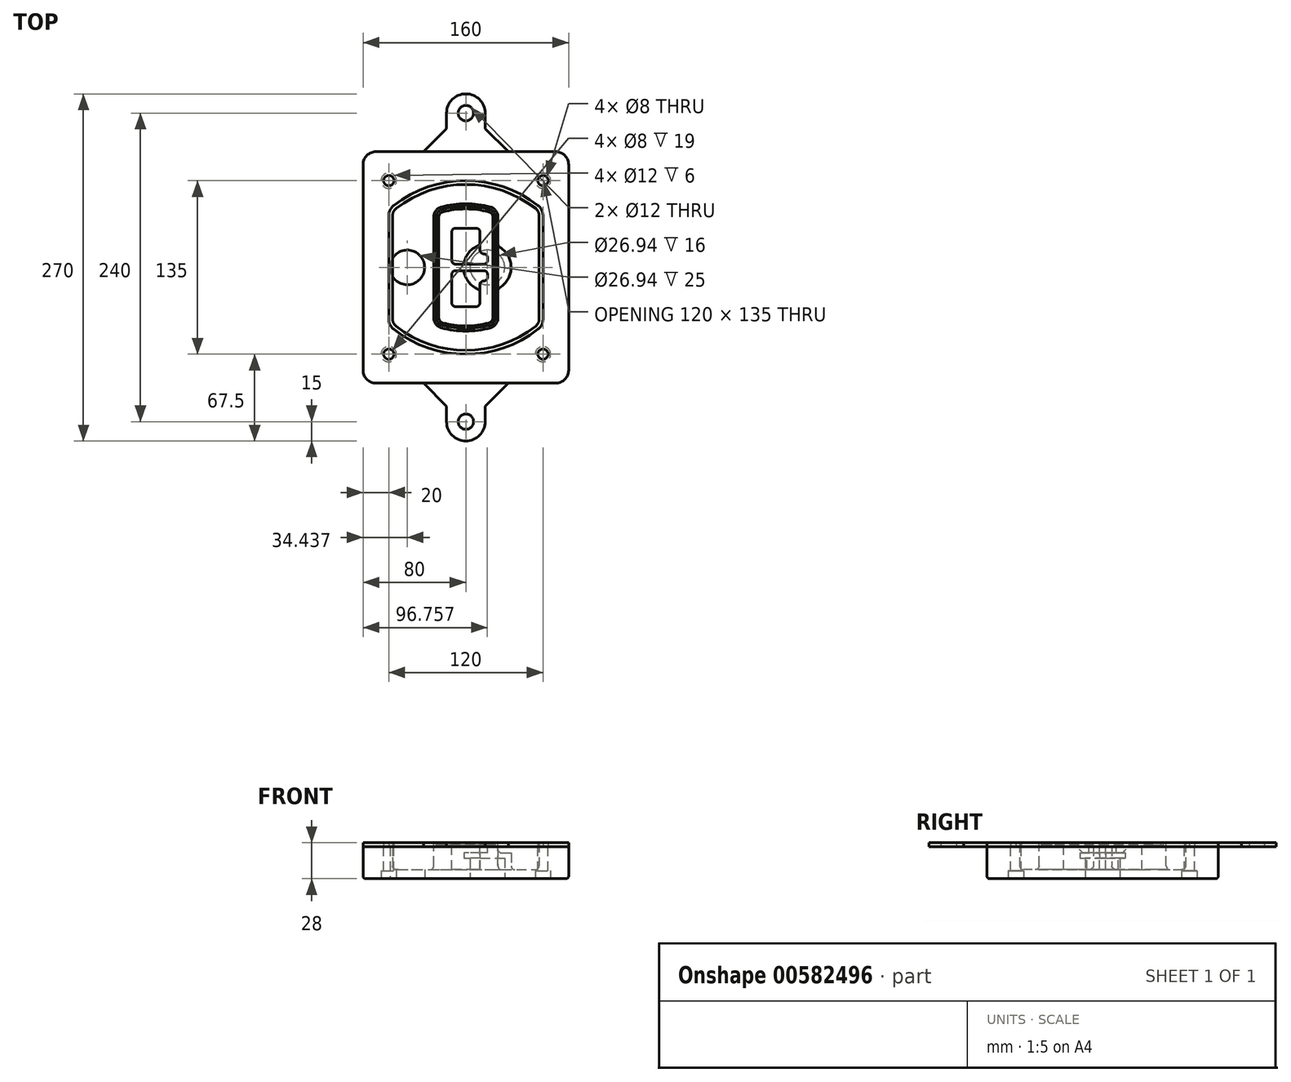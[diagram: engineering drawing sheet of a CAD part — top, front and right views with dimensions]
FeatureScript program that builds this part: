
annotation { "Feature Type Name" : "Feature", "Feature Type Description" : "" }
export const myFeature = defineFeature(function(context is Context, id is Id, definition is map)
    precondition{}
    {
        {
            var Q0;
            Q0=qCreatedBy(makeId("Top.planeOp"),FACE);
            var sketch = newSketch(context, id + "F0", { "sketchPlane" : qUnion([Q0])});
            skPoint(sketch, "E0.rect.middle", {"position": v(0, 0) * mm});
            skLineSegment(sketch, "E1.bottom", {"start": v(-70, -90) * mm, "end": v(70, -90) * mm});
            skLineSegment(sketch, "E1.top", {"start": v(-70, 90) * mm, "end": v(70, 90) * mm});
            skLineSegment(sketch, "E1.left", {"start": v(-80, -80) * mm, "end": v(-80, 80) * mm});
            skLineSegment(sketch, "E1.right", {"start": v(80, -80) * mm, "end": v(80, 80) * mm});
            skLineSegment(sketch, "E2", {"start": v(-80, 90) * mm, "end": v(80, -90) * mm, "construction": true});
            skLineSegment(sketch, "E3", {"start": v(80, 90) * mm, "end": v(-80, -90) * mm, "construction": true});
            skCircle(sketch, "E4", {"center": v(-60, 67.5) * mm, "radius": 4 * mm});
            skCircle(sketch, "E5", {"center": v(60, 67.5) * mm, "radius": 4 * mm});
            skCircle(sketch, "E6", {"center": v(60, -67.5) * mm, "radius": 4 * mm});
            skCircle(sketch, "E7", {"center": v(-60, -67.5) * mm, "radius": 4 * mm});
            skLineSegment(sketch, "E8", {"start": v(-60, 67.5) * mm, "end": v(60, 67.5) * mm, "construction": true});
            skLineSegment(sketch, "E9", {"start": v(60, 67.5) * mm, "end": v(60, -67.5) * mm, "construction": true});
            skLineSegment(sketch, "E10", {"start": v(60, -67.5) * mm, "end": v(-60, -67.5) * mm, "construction": true});
            skLineSegment(sketch, "E11", {"start": v(-60, -67.5) * mm, "end": v(-60, 67.5) * mm, "construction": true});
            skLineSegment(sketch, "E12", {"start": v(-60, 40.3) * mm, "end": v(-60, -40.3) * mm});
            skLineSegment(sketch, "E13", {"start": v(60, 40.3) * mm, "end": v(60, -40.3) * mm});
            skArc(sketch, "E14", {"start": v(56.15, 48.18) * mm, "mid": v(0, 67.5) * mm, "end": v(-56.15, 48.18) * mm});
            skArc(sketch, "E15", {"start": v(-56.15, -48.18) * mm, "mid": v(0, -67.5) * mm, "end": v(56.15, -48.18) * mm});
            skLineSegment(sketch, "E16", {"start": v(-60, 0) * mm, "end": v(60, 0) * mm, "construction": true});
            skPoint(sketch, "E17.visualSharp", {"position": v(-60, -45) * mm});
            skArc(sketch, "E17.filletArc", {"start": v(-60, -40.3) * mm, "mid": v(-58.99, -44.68) * mm, "end": v(-56.15, -48.18) * mm});
            skPoint(sketch, "E18.visualSharp", {"position": v(-60, 45) * mm});
            skArc(sketch, "E18.filletArc", {"start": v(-56.15, 48.18) * mm, "mid": v(-58.99, 44.68) * mm, "end": v(-60, 40.3) * mm});
            skPoint(sketch, "E19.visualSharp", {"position": v(60, 45) * mm});
            skArc(sketch, "E19.filletArc", {"start": v(60, 40.3) * mm, "mid": v(58.99, 44.68) * mm, "end": v(56.15, 48.18) * mm});
            skPoint(sketch, "E20.visualSharp", {"position": v(60, -45) * mm});
            skArc(sketch, "E20.filletArc", {"start": v(56.15, -48.18) * mm, "mid": v(58.99, -44.68) * mm, "end": v(60, -40.3) * mm});
            skPoint(sketch, "E21.visualSharp", {"position": v(-80, 90) * mm});
            skArc(sketch, "E21.filletArc", {"start": v(-70, 90) * mm, "mid": v(-77.07, 87.07) * mm, "end": v(-80, 80) * mm});
            skPoint(sketch, "E22.visualSharp", {"position": v(80, 90) * mm});
            skArc(sketch, "E22.filletArc", {"start": v(80, 80) * mm, "mid": v(77.07, 87.07) * mm, "end": v(70, 90) * mm});
            skPoint(sketch, "E23.visualSharp", {"position": v(80, -90) * mm});
            skArc(sketch, "E23.filletArc", {"start": v(70, -90) * mm, "mid": v(77.07, -87.07) * mm, "end": v(80, -80) * mm});
            skPoint(sketch, "E24.visualSharp", {"position": v(-80, -90) * mm});
            skArc(sketch, "E24.filletArc", {"start": v(-80, -80) * mm, "mid": v(-77.07, -87.07) * mm, "end": v(-70, -90) * mm});
            skArc(sketch, "E25.0", {"start": v(57, 40.3) * mm, "mid": v(56.3, 43.36) * mm, "end": v(54.3, 45.81) * mm});
            skLineSegment(sketch, "E25.1", {"start": v(57, 40.3) * mm, "end": v(57, -40.3) * mm});
            skArc(sketch, "E25.2", {"start": v(54.3, -45.81) * mm, "mid": v(56.3, -43.36) * mm, "end": v(57, -40.3) * mm});
            skArc(sketch, "E25.3", {"start": v(-54.3, -45.81) * mm, "mid": v(0, -64.5) * mm, "end": v(54.3, -45.81) * mm});
            skArc(sketch, "E25.4", {"start": v(-57, -40.3) * mm, "mid": v(-56.3, -43.36) * mm, "end": v(-54.3, -45.81) * mm});
            skArc(sketch, "E25.5", {"start": v(54.3, 45.81) * mm, "mid": v(0, 64.5) * mm, "end": v(-54.3, 45.81) * mm});
            skLineSegment(sketch, "E25.6", {"start": v(-57, 40.3) * mm, "end": v(-57, -40.3) * mm});
            skArc(sketch, "E25.7", {"start": v(-54.3, 45.81) * mm, "mid": v(-56.3, 43.36) * mm, "end": v(-57, 40.3) * mm});
            skArc(sketch, "E26.0", {"start": v(-58.62, 51.33) * mm, "mid": v(-62.58, 46.43) * mm, "end": v(-64, 40.3) * mm});
            skArc(sketch, "E26.1", {"start": v(58.62, 51.33) * mm, "mid": v(0, 71.5) * mm, "end": v(-58.62, 51.33) * mm});
            skArc(sketch, "E26.2", {"start": v(64, 40.3) * mm, "mid": v(62.58, 46.43) * mm, "end": v(58.62, 51.33) * mm});
            skLineSegment(sketch, "E26.3", {"start": v(64, 40.3) * mm, "end": v(64, -40.3) * mm});
            skArc(sketch, "E26.4", {"start": v(58.62, -51.33) * mm, "mid": v(62.58, -46.43) * mm, "end": v(64, -40.3) * mm});
            skLineSegment(sketch, "E26.5", {"start": v(-64, 40.3) * mm, "end": v(-64, -40.3) * mm});
            skArc(sketch, "E26.6", {"start": v(-58.62, -51.33) * mm, "mid": v(0, -71.5) * mm, "end": v(58.62, -51.33) * mm});
            skArc(sketch, "E26.7", {"start": v(-64, -40.3) * mm, "mid": v(-62.58, -46.43) * mm, "end": v(-58.62, -51.33) * mm});
            skSolve(sketch);
        }
        {
            var Q0;
            Q0=makeQuery(id+"F0.imprint","IMPRINT",FACE,{"disambiguationData":[TD([[makeQuery(id+"F0.imprint","IMPRINT",EDGE,{"derivedFrom":sQuery(id+"F0.wireOp",EDGE,"E1.bottom")}),1.0]])]});
            var Q1;
            Q1=makeQuery(id+"F0.imprint","IMPRINT",FACE,{"disambiguationData":[TD([[makeQuery(id+"F0.imprint","IMPRINT",EDGE,{"derivedFrom":sQuery(id+"F0.wireOp",EDGE,"E12")}),1.0]])]});
            var Q2;
            Q2=makeQuery(id+"F0.imprint","IMPRINT",FACE,{"disambiguationData":[TD([[makeQuery(id+"F0.imprint","IMPRINT",EDGE,{"derivedFrom":sQuery(id+"F0.wireOp",EDGE,"E25.0")}),1.0]])]});
            var Q3;
            Q3=makeQuery(id+"F0.imprint","IMPRINT",FACE,{"disambiguationData":[TD([[makeQuery(id+"F0.imprint","IMPRINT",EDGE,{"derivedFrom":sQuery(id+"F0.wireOp",EDGE,"E12")}),-1.0]])]});
            extrude(context, id + "F1", {"entities" : qUnion([Q0, Q1, Q2, Q3]), "oppositeDirection" : true, "depth" : 25 * mm});
        }
        {
            var Q0;
            Q0=makeQuery(id+"F0.imprint","IMPRINT",FACE,{"disambiguationData":[TD([[makeQuery(id+"F0.imprint","IMPRINT",EDGE,{"derivedFrom":sQuery(id+"F0.wireOp",EDGE,"E12")}),1.0]])]});
            extrude(context, id + "F2", {"entities" : qUnion([Q0]), "operationType" : NewBodyOperationType.ADD, "depth" : 3 * mm});
        }
        {
            var Q0;
            Q0=makeQuery(id+"F0.imprint","IMPRINT",FACE,{"disambiguationData":[TD([[makeQuery(id+"F0.imprint","IMPRINT",EDGE,{"derivedFrom":sQuery(id+"F0.wireOp",EDGE,"E25.0")}),1.0]])]});
            extrude(context, id + "F3", {"entities" : qUnion([Q0]), "operationType" : NewBodyOperationType.REMOVE, "oppositeDirection" : true, "depth" : 18 * mm});
        }
        {
            var Q0;
            Q0=makeQuery(id+"F2.opExtrude","CAP_FACE",FACE,{"disambiguationData":[OSD([sQuery(id+"F0.wireOp",EDGE,"E12"),sQuery(id+"F0.wireOp",EDGE,"E13"),sQuery(id+"F0.wireOp",EDGE,"E14"),sQuery(id+"F0.wireOp",EDGE,"E15"),sQuery(id+"F0.wireOp",EDGE,"E17.filletArc"),sQuery(id+"F0.wireOp",EDGE,"E18.filletArc"),sQuery(id+"F0.wireOp",EDGE,"E19.filletArc"),sQuery(id+"F0.wireOp",EDGE,"E20.filletArc"),sQuery(id+"F0.wireOp",EDGE,"E25.0"),sQuery(id+"F0.wireOp",EDGE,"E25.1"),sQuery(id+"F0.wireOp",EDGE,"E25.2"),sQuery(id+"F0.wireOp",EDGE,"E25.3"),sQuery(id+"F0.wireOp",EDGE,"E25.4"),sQuery(id+"F0.wireOp",EDGE,"E25.5"),sQuery(id+"F0.wireOp",EDGE,"E25.6"),sQuery(id+"F0.wireOp",EDGE,"E25.7")])],"isStart":false});
            var sketch = newSketch(context, id + "F4", { "sketchPlane" : qUnion([Q0])});
            skArc(sketch, "E27.0", {"start": v(-19.08, -46.97) * mm, "mid": v(0, -49.5) * mm, "end": v(19.08, -46.97) * mm});
            skArc(sketch, "E28.0", {"start": v(19.08, 46.97) * mm, "mid": v(0, 49.5) * mm, "end": v(-19.08, 46.97) * mm});
            skLineSegment(sketch, "E29", {"start": v(-25, 39.25) * mm, "end": v(-25, -39.25) * mm});
            skLineSegment(sketch, "E30", {"start": v(25, 39.25) * mm, "end": v(25, -39.25) * mm});
            skLineSegment(sketch, "E31", {"start": v(-25, 45.1) * mm, "end": v(25, 45.1) * mm, "construction": true});
            skLineSegment(sketch, "E32", {"start": v(-25, -45.1) * mm, "end": v(25, -45.1) * mm, "construction": true});
            skPoint(sketch, "E33.visualSharp", {"position": v(-25, 45.1) * mm});
            skArc(sketch, "E33.filletArc", {"start": v(-19.08, 46.97) * mm, "mid": v(-23.35, 44.11) * mm, "end": v(-25, 39.25) * mm});
            skPoint(sketch, "E34.visualSharp", {"position": v(25, 45.1) * mm});
            skArc(sketch, "E34.filletArc", {"start": v(25, 39.25) * mm, "mid": v(23.35, 44.11) * mm, "end": v(19.08, 46.97) * mm});
            skPoint(sketch, "E35.visualSharp", {"position": v(25, -45.1) * mm});
            skArc(sketch, "E35.filletArc", {"start": v(19.08, -46.97) * mm, "mid": v(23.35, -44.11) * mm, "end": v(25, -39.25) * mm});
            skPoint(sketch, "E36.visualSharp", {"position": v(-25, -45.1) * mm});
            skArc(sketch, "E36.filletArc", {"start": v(-25, -39.25) * mm, "mid": v(-23.35, -44.11) * mm, "end": v(-19.08, -46.97) * mm});
            skArc(sketch, "E37.0", {"start": v(54.3, 45.81) * mm, "mid": v(0, 64.5) * mm, "end": v(-54.3, 45.81) * mm});
            skArc(sketch, "E37.1", {"start": v(-54.3, 45.81) * mm, "mid": v(-56.3, 43.36) * mm, "end": v(-57, 40.3) * mm});
            skLineSegment(sketch, "E37.2", {"start": v(-57, 40.3) * mm, "end": v(-57, -40.3) * mm});
            skArc(sketch, "E37.3", {"start": v(-57, -40.3) * mm, "mid": v(-56.3, -43.36) * mm, "end": v(-54.3, -45.81) * mm});
            skArc(sketch, "E37.4", {"start": v(-54.3, -45.81) * mm, "mid": v(0, -64.5) * mm, "end": v(54.3, -45.81) * mm});
            skArc(sketch, "E37.5", {"start": v(54.3, -45.81) * mm, "mid": v(56.3, -43.36) * mm, "end": v(57, -40.3) * mm});
            skLineSegment(sketch, "E37.6", {"start": v(57, 40.3) * mm, "end": v(57, -40.3) * mm});
            skArc(sketch, "E37.7", {"start": v(57, 40.3) * mm, "mid": v(56.3, 43.36) * mm, "end": v(54.3, 45.81) * mm});
            skLineSegment(sketch, "E38.0", {"start": v(23, 39.25) * mm, "end": v(23, -39.25) * mm});
            skArc(sketch, "E38.1", {"start": v(18.56, -45.04) * mm, "mid": v(21.76, -42.9) * mm, "end": v(23, -39.25) * mm});
            skArc(sketch, "E38.2", {"start": v(-18.56, -45.04) * mm, "mid": v(0, -47.5) * mm, "end": v(18.56, -45.04) * mm});
            skArc(sketch, "E38.3", {"start": v(-23, -39.25) * mm, "mid": v(-21.76, -42.9) * mm, "end": v(-18.56, -45.04) * mm});
            skLineSegment(sketch, "E38.4", {"start": v(-23, 39.25) * mm, "end": v(-23, -39.25) * mm});
            skArc(sketch, "E38.5", {"start": v(23, 39.25) * mm, "mid": v(21.76, 42.9) * mm, "end": v(18.56, 45.04) * mm});
            skArc(sketch, "E38.6", {"start": v(-18.56, 45.04) * mm, "mid": v(-21.76, 42.9) * mm, "end": v(-23, 39.25) * mm});
            skArc(sketch, "E38.7", {"start": v(18.56, 45.04) * mm, "mid": v(0, 47.5) * mm, "end": v(-18.56, 45.04) * mm});
            skArc(sketch, "E39.0", {"start": v(21, 39.25) * mm, "mid": v(20.18, 41.68) * mm, "end": v(18.04, 43.1) * mm});
            skLineSegment(sketch, "E39.1", {"start": v(21, 39.25) * mm, "end": v(21, -39.25) * mm});
            skArc(sketch, "E39.2", {"start": v(18.04, -43.1) * mm, "mid": v(20.18, -41.68) * mm, "end": v(21, -39.25) * mm});
            skArc(sketch, "E39.3", {"start": v(-18.04, -43.1) * mm, "mid": v(0, -45.5) * mm, "end": v(18.04, -43.1) * mm});
            skArc(sketch, "E39.4", {"start": v(-21, -39.25) * mm, "mid": v(-20.18, -41.68) * mm, "end": v(-18.04, -43.1) * mm});
            skArc(sketch, "E39.5", {"start": v(18.04, 43.1) * mm, "mid": v(0, 45.5) * mm, "end": v(-18.04, 43.1) * mm});
            skLineSegment(sketch, "E39.6", {"start": v(-21, 39.25) * mm, "end": v(-21, -39.25) * mm});
            skArc(sketch, "E39.7", {"start": v(-18.04, 43.1) * mm, "mid": v(-20.18, 41.68) * mm, "end": v(-21, 39.25) * mm});
            skLineSegment(sketch, "E40", {"start": v(-25, 0) * mm, "end": v(25, 0) * mm, "construction": true});
            skLineSegment(sketch, "E41", {"start": v(-11, 5.5) * mm, "end": v(-11, 27.5) * mm});
            skLineSegment(sketch, "E42", {"start": v(-8, 30.5) * mm, "end": v(8, 30.5) * mm});
            skLineSegment(sketch, "E43", {"start": v(11, 27.5) * mm, "end": v(11, 13.5) * mm});
            skLineSegment(sketch, "E44", {"start": v(14, 10.5) * mm, "end": v(14, 10.5) * mm});
            skLineSegment(sketch, "E45", {"start": v(17, 7.5) * mm, "end": v(17, 5.5) * mm});
            skLineSegment(sketch, "E46", {"start": v(14, 2.5) * mm, "end": v(-8, 2.5) * mm});
            skPoint(sketch, "E47.visualSharp", {"position": v(-11, 30.5) * mm});
            skArc(sketch, "E47.filletArc", {"start": v(-8, 30.5) * mm, "mid": v(-10.12, 29.62) * mm, "end": v(-11, 27.5) * mm});
            skPoint(sketch, "E48.visualSharp", {"position": v(11, 30.5) * mm});
            skArc(sketch, "E48.filletArc", {"start": v(11, 27.5) * mm, "mid": v(10.12, 29.62) * mm, "end": v(8, 30.5) * mm});
            skPoint(sketch, "E49.visualSharp", {"position": v(11, 10.5) * mm});
            skArc(sketch, "E49.filletArc", {"start": v(11, 13.5) * mm, "mid": v(11.88, 11.38) * mm, "end": v(14, 10.5) * mm});
            skPoint(sketch, "E50.visualSharp", {"position": v(17, 10.5) * mm});
            skArc(sketch, "E50.filletArc", {"start": v(17, 7.5) * mm, "mid": v(16.12, 9.62) * mm, "end": v(14, 10.5) * mm});
            skPoint(sketch, "E51.visualSharp", {"position": v(17, 2.5) * mm});
            skArc(sketch, "E51.filletArc", {"start": v(14, 2.5) * mm, "mid": v(16.12, 3.38) * mm, "end": v(17, 5.5) * mm});
            skPoint(sketch, "E52.visualSharp", {"position": v(-11, 2.5) * mm});
            skArc(sketch, "E52.filletArc", {"start": v(-11, 5.5) * mm, "mid": v(-10.12, 3.38) * mm, "end": v(-8, 2.5) * mm});
            skLineSegment(sketch, "E53.0.MirrorCS", {"start": v(14, -2.5) * mm, "end": v(-8, -2.5) * mm});
            skArc(sketch, "E54.0.MirrorCS", {"start": v(-11, -5.5) * mm, "mid": v(-10.12, -3.38) * mm, "end": v(-8, -2.5) * mm});
            skLineSegment(sketch, "E55.0.MirrorCS", {"start": v(-11, -5.5) * mm, "end": v(-11, -27.5) * mm});
            skArc(sketch, "E56.0.MirrorCS", {"start": v(-8, -30.5) * mm, "mid": v(-10.12, -29.62) * mm, "end": v(-11, -27.5) * mm});
            skLineSegment(sketch, "E57.0.MirrorCS", {"start": v(-8, -30.5) * mm, "end": v(8, -30.5) * mm});
            skArc(sketch, "E58.0.MirrorCS", {"start": v(11, -27.5) * mm, "mid": v(10.12, -29.62) * mm, "end": v(8, -30.5) * mm});
            skLineSegment(sketch, "E59.0.MirrorCS", {"start": v(11, -27.5) * mm, "end": v(11, -13.5) * mm});
            skArc(sketch, "E60.0.MirrorCS", {"start": v(11, -13.5) * mm, "mid": v(11.88, -11.38) * mm, "end": v(14, -10.5) * mm});
            skArc(sketch, "E61.0.MirrorCS", {"start": v(17, -7.5) * mm, "mid": v(16.12, -9.62) * mm, "end": v(14, -10.5) * mm});
            skLineSegment(sketch, "E62.0.MirrorCS", {"start": v(17, -7.5) * mm, "end": v(17, -5.5) * mm});
            skArc(sketch, "E63.0.MirrorCS", {"start": v(14, -2.5) * mm, "mid": v(16.12, -3.38) * mm, "end": v(17, -5.5) * mm});
            skSolve(sketch);
        }
        {
            var Q0;
            Q0=makeQuery(id+"F4.imprint","IMPRINT",FACE,{"disambiguationData":[TD([[makeQuery(id+"F4.imprint","IMPRINT",EDGE,{"derivedFrom":sQuery(id+"F4.wireOp",EDGE,"E27.0")}),1.0]])]});
            var Q1;
            Q1=makeQuery(id+"F4.imprint","IMPRINT",FACE,{"disambiguationData":[TD([[makeQuery(id+"F4.imprint","IMPRINT",EDGE,{"derivedFrom":sQuery(id+"F4.wireOp",EDGE,"E38.0")}),-1.0]])]});
            var Q2;
            Q2=makeQuery(id+"F4.imprint","IMPRINT",FACE,{"disambiguationData":[TD([[makeQuery(id+"F4.imprint","IMPRINT",EDGE,{"derivedFrom":sQuery(id+"F4.wireOp",EDGE,"E39.0")}),1.0]])]});
            extrude(context, id + "F5", {"entities" : qUnion([Q0, Q1, Q2]), "operationType" : NewBodyOperationType.ADD, "endBound" : BoundingType.UP_TO_NEXT, "oppositeDirection" : true, "depth" : 25 * mm});
        }
        {
            var Q0;
            Q0=makeQuery(id+"F4.imprint","IMPRINT",FACE,{"disambiguationData":[TD([[makeQuery(id+"F4.imprint","IMPRINT",EDGE,{"derivedFrom":sQuery(id+"F4.wireOp",EDGE,"E38.0")}),-1.0]])]});
            extrude(context, id + "F6", {"entities" : qUnion([Q0]), "operationType" : NewBodyOperationType.REMOVE, "oppositeDirection" : true, "depth" : 2 * mm});
        }
        {
            var Q0;
            Q0=makeQuery(id+"F1.opExtrude","CAP_FACE",FACE,{"disambiguationData":[OSD([sQuery(id+"F0.wireOp",EDGE,"E1.bottom"),sQuery(id+"F0.wireOp",EDGE,"E1.top"),sQuery(id+"F0.wireOp",EDGE,"E1.left"),sQuery(id+"F0.wireOp",EDGE,"E1.right"),sQuery(id+"F0.wireOp",EDGE,"E4"),sQuery(id+"F0.wireOp",EDGE,"E5"),sQuery(id+"F0.wireOp",EDGE,"E6"),sQuery(id+"F0.wireOp",EDGE,"E7"),sQuery(id+"F0.wireOp",EDGE,"E21.filletArc"),sQuery(id+"F0.wireOp",EDGE,"E22.filletArc"),sQuery(id+"F0.wireOp",EDGE,"E23.filletArc"),sQuery(id+"F0.wireOp",EDGE,"E24.filletArc")])],"isStart":false});
            var sketch = newSketch(context, id + "F7", { "sketchPlane" : qUnion([Q0])});
            skCircle(sketch, "E64", {"center": v(16.76, 0) * mm, "radius": 13.47 * mm});
            skCircle(sketch, "E65", {"center": v(-45.56, 0) * mm, "radius": 13.47 * mm});
            skLineSegment(sketch, "E66", {"start": v(80, 0) * mm, "end": v(-80, 0) * mm});
            skCircle(sketch, "E67", {"center": v(16.76, 0) * mm, "radius": 18.47 * mm});
            skCircle(sketch, "E68", {"center": v(60, -67.5) * mm, "radius": 6 * mm});
            skCircle(sketch, "E69", {"center": v(-60, -67.5) * mm, "radius": 6 * mm});
            skCircle(sketch, "E70", {"center": v(-60, 67.5) * mm, "radius": 6 * mm});
            skCircle(sketch, "E71", {"center": v(60, 67.5) * mm, "radius": 6 * mm});
            skSolve(sketch);
        }
        {
            var Q0;
            {var subQ1=sQuery(id+"F7.wireOp",EDGE,"E66");var subQ4=sQuery(id+"F7.wireOp",EDGE,"E64");var subQ6=makeQuery(id+"F7.imprint","INTERSECT",VERTEX,{"disambiguationData":[OD(0.0)],"derivedFrom":[subQ4,subQ1]});Q0=makeQuery(id+"F7.imprint","IMPRINT",FACE,{"disambiguationData":[TD([[makeQuery(id+"F7.imprint","IMPRINT",EDGE,{"disambiguationData":[TD([[subQ6,-1.0]])],"derivedFrom":subQ4}),-1.0]])]});}
            var Q1;
            {var subQ0=sQuery(id+"F7.wireOp",EDGE,"E66");var subQ1=sQuery(id+"F7.wireOp",EDGE,"E64");var subQ3=makeQuery(id+"F7.imprint","INTERSECT",VERTEX,{"disambiguationData":[OD(0.0)],"derivedFrom":[subQ1,subQ0]});Q1=makeQuery(id+"F7.imprint","IMPRINT",FACE,{"disambiguationData":[TD([[makeQuery(id+"F7.imprint","IMPRINT",EDGE,{"disambiguationData":[TD([[subQ3,-1.0]])],"derivedFrom":subQ1}),1.0]])]});}
            var Q2;
            {var subQ0=sQuery(id+"F7.wireOp",EDGE,"E66");var subQ1=sQuery(id+"F7.wireOp",EDGE,"E64");var subQ3=makeQuery(id+"F7.imprint","INTERSECT",VERTEX,{"disambiguationData":[OD(0.0)],"derivedFrom":[subQ1,subQ0]});Q2=makeQuery(id+"F7.imprint","IMPRINT",FACE,{"disambiguationData":[TD([[makeQuery(id+"F7.imprint","IMPRINT",EDGE,{"disambiguationData":[TD([[subQ3,1.0]])],"derivedFrom":subQ1}),1.0]])]});}
            var Q3;
            {var subQ1=sQuery(id+"F7.wireOp",EDGE,"E66");var subQ4=sQuery(id+"F7.wireOp",EDGE,"E64");var subQ6=makeQuery(id+"F7.imprint","INTERSECT",VERTEX,{"disambiguationData":[OD(0.0)],"derivedFrom":[subQ4,subQ1]});Q3=makeQuery(id+"F7.imprint","IMPRINT",FACE,{"disambiguationData":[TD([[makeQuery(id+"F7.imprint","IMPRINT",EDGE,{"disambiguationData":[TD([[subQ6,1.0]])],"derivedFrom":subQ4}),-1.0]])]});}
            extrude(context, id + "F8", {"entities" : qUnion([Q0, Q1, Q2, Q3]), "operationType" : NewBodyOperationType.ADD, "oppositeDirection" : true, "depth" : 20 * mm});
        }
        {
            var Q0;
            {var subQ0=sQuery(id+"F7.wireOp",EDGE,"E66");var subQ1=sQuery(id+"F7.wireOp",EDGE,"E64");var subQ3=makeQuery(id+"F7.imprint","INTERSECT",VERTEX,{"disambiguationData":[OD(0.0)],"derivedFrom":[subQ1,subQ0]});Q0=makeQuery(id+"F7.imprint","IMPRINT",FACE,{"disambiguationData":[TD([[makeQuery(id+"F7.imprint","IMPRINT",EDGE,{"disambiguationData":[TD([[subQ3,-1.0]])],"derivedFrom":subQ1}),1.0]])]});}
            var Q1;
            {var subQ0=sQuery(id+"F7.wireOp",EDGE,"E66");var subQ1=sQuery(id+"F7.wireOp",EDGE,"E64");var subQ3=makeQuery(id+"F7.imprint","INTERSECT",VERTEX,{"disambiguationData":[OD(0.0)],"derivedFrom":[subQ1,subQ0]});Q1=makeQuery(id+"F7.imprint","IMPRINT",FACE,{"disambiguationData":[TD([[makeQuery(id+"F7.imprint","IMPRINT",EDGE,{"disambiguationData":[TD([[subQ3,1.0]])],"derivedFrom":subQ1}),1.0]])]});}
            extrude(context, id + "F9", {"entities" : qUnion([Q0, Q1]), "operationType" : NewBodyOperationType.REMOVE, "oppositeDirection" : true, "depth" : 16 * mm});
        }
        {
            var Q0;
            {var subQ0=sQuery(id+"F7.wireOp",EDGE,"E66");var subQ1=sQuery(id+"F7.wireOp",EDGE,"E65");var subQ3=makeQuery(id+"F7.imprint","INTERSECT",VERTEX,{"disambiguationData":[OD(0.0)],"derivedFrom":[subQ1,subQ0]});Q0=makeQuery(id+"F7.imprint","IMPRINT",FACE,{"disambiguationData":[TD([[makeQuery(id+"F7.imprint","IMPRINT",EDGE,{"disambiguationData":[TD([[subQ3,-1.0]])],"derivedFrom":subQ1}),1.0]])]});}
            var Q1;
            {var subQ0=sQuery(id+"F7.wireOp",EDGE,"E66");var subQ1=sQuery(id+"F7.wireOp",EDGE,"E65");var subQ3=makeQuery(id+"F7.imprint","INTERSECT",VERTEX,{"disambiguationData":[OD(0.0)],"derivedFrom":[subQ1,subQ0]});Q1=makeQuery(id+"F7.imprint","IMPRINT",FACE,{"disambiguationData":[TD([[makeQuery(id+"F7.imprint","IMPRINT",EDGE,{"disambiguationData":[TD([[subQ3,1.0]])],"derivedFrom":subQ1}),1.0]])]});}
            extrude(context, id + "F10", {"entities" : qUnion([Q0, Q1]), "operationType" : NewBodyOperationType.REMOVE, "oppositeDirection" : true, "depth" : 25 * mm});
        }
        {
            var Q0;
            Q0=makeQuery(id+"F7.imprint","IMPRINT",FACE,{"disambiguationData":[TD([[makeQuery(id+"F7.imprint","IMPRINT",EDGE,{"derivedFrom":sQuery(id+"F7.wireOp",EDGE,"E68")}),1.0]])]});
            var Q1;
            Q1=makeQuery(id+"F7.imprint","IMPRINT",FACE,{"disambiguationData":[TD([[makeQuery(id+"F7.imprint","IMPRINT",EDGE,{"derivedFrom":makeQuery(id+"F1.opExtrude","CAP_EDGE",EDGE,{"disambiguationData":[OSD([sQuery(id+"F0.wireOp",EDGE,"E5")])],"isStart":false})}),-1.0]])]});
            var Q2;
            Q2=makeQuery(id+"F7.imprint","IMPRINT",FACE,{"disambiguationData":[TD([[makeQuery(id+"F7.imprint","IMPRINT",EDGE,{"derivedFrom":sQuery(id+"F7.wireOp",EDGE,"E69")}),1.0]])]});
            var Q3;
            Q3=makeQuery(id+"F7.imprint","IMPRINT",FACE,{"disambiguationData":[TD([[makeQuery(id+"F7.imprint","IMPRINT",EDGE,{"derivedFrom":makeQuery(id+"F1.opExtrude","CAP_EDGE",EDGE,{"disambiguationData":[OSD([sQuery(id+"F0.wireOp",EDGE,"E4")])],"isStart":false})}),-1.0]])]});
            var Q4;
            Q4=makeQuery(id+"F7.imprint","IMPRINT",FACE,{"disambiguationData":[TD([[makeQuery(id+"F7.imprint","IMPRINT",EDGE,{"derivedFrom":sQuery(id+"F7.wireOp",EDGE,"E70")}),1.0]])]});
            var Q5;
            Q5=makeQuery(id+"F7.imprint","IMPRINT",FACE,{"disambiguationData":[TD([[makeQuery(id+"F7.imprint","IMPRINT",EDGE,{"derivedFrom":makeQuery(id+"F1.opExtrude","CAP_EDGE",EDGE,{"disambiguationData":[OSD([sQuery(id+"F0.wireOp",EDGE,"E7")])],"isStart":false})}),-1.0]])]});
            var Q6;
            Q6=makeQuery(id+"F7.imprint","IMPRINT",FACE,{"disambiguationData":[TD([[makeQuery(id+"F7.imprint","IMPRINT",EDGE,{"derivedFrom":sQuery(id+"F7.wireOp",EDGE,"E71")}),1.0]])]});
            var Q7;
            Q7=makeQuery(id+"F7.imprint","IMPRINT",FACE,{"disambiguationData":[TD([[makeQuery(id+"F7.imprint","IMPRINT",EDGE,{"derivedFrom":makeQuery(id+"F1.opExtrude","CAP_EDGE",EDGE,{"disambiguationData":[OSD([sQuery(id+"F0.wireOp",EDGE,"E6")])],"isStart":false})}),-1.0]])]});
            extrude(context, id + "F11", {"entities" : qUnion([Q0, Q1, Q2, Q3, Q4, Q5, Q6, Q7]), "operationType" : NewBodyOperationType.REMOVE, "oppositeDirection" : true, "depth" : 6 * mm});
        }
        {
            var Q0;
            Q0=makeQuery(id+"F9.boolean.opBoolean","COPY",FACE,{"derivedFrom":makeQuery(id+"F9.opExtrude","CAP_FACE",FACE,{"disambiguationData":[OSD([sQuery(id+"F7.wireOp",EDGE,"E64")])],"isStart":false})});
            var sketch = newSketch(context, id + "F12", { "sketchPlane" : qUnion([Q0])});
            skArc(sketch, "E72.0", {"start": v(11, 17.55) * mm, "mid": v(2.57, 11.82) * mm, "end": v(-1.54, 2.5) * mm});
            skArc(sketch, "E72.1", {"start": v(-1.54, -2.5) * mm, "mid": v(2.57, -11.82) * mm, "end": v(11, -17.55) * mm});
            skLineSegment(sketch, "E73", {"start": v(-1.54, -2.5) * mm, "end": v(14, -2.5) * mm});
            skLineSegment(sketch, "E74.0", {"start": v(14, 2.5) * mm, "end": v(-1.54, 2.5) * mm});
            skArc(sketch, "E74.1", {"start": v(14, 2.5) * mm, "mid": v(16.12, 3.38) * mm, "end": v(17, 5.5) * mm});
            skLineSegment(sketch, "E74.2", {"start": v(17, 7.5) * mm, "end": v(17, 5.5) * mm});
            skArc(sketch, "E74.3", {"start": v(17, 7.5) * mm, "mid": v(16.12, 9.62) * mm, "end": v(14, 10.5) * mm});
            skArc(sketch, "E74.4", {"start": v(11, 13.5) * mm, "mid": v(11.88, 11.38) * mm, "end": v(14, 10.5) * mm});
            skLineSegment(sketch, "E74.5", {"start": v(11, 17.55) * mm, "end": v(11, 13.5) * mm});
            skLineSegment(sketch, "E74.7", {"start": v(14, -2.5) * mm, "end": v(-1.54, -2.5) * mm});
            skArc(sketch, "E74.8", {"start": v(14, -2.5) * mm, "mid": v(16.12, -3.38) * mm, "end": v(17, -5.5) * mm});
            skLineSegment(sketch, "E74.9", {"start": v(17, -7.5) * mm, "end": v(17, -5.5) * mm});
            skArc(sketch, "E74.10", {"start": v(17, -7.5) * mm, "mid": v(16.12, -9.62) * mm, "end": v(14, -10.5) * mm});
            skArc(sketch, "E74.11", {"start": v(11, -13.5) * mm, "mid": v(11.88, -11.38) * mm, "end": v(14, -10.5) * mm});
            skLineSegment(sketch, "E74.12", {"start": v(11, -17.55) * mm, "end": v(11, -13.5) * mm});
            skPoint(sketch, "E75.orphan", {"position": v(11, -27.5) * mm});
            skPoint(sketch, "E76.orphan", {"position": v(-8, -2.5) * mm});
            skPoint(sketch, "E77.orphan", {"position": v(-8, 2.5) * mm});
            skPoint(sketch, "E78.orphan", {"position": v(11, 27.5) * mm});
            skSolve(sketch);
        }
        {
            var Q0;
            {var subQ7=sQuery(id+"F12.wireOp",EDGE,"E72.0");var subQ14=sQuery(id+"F12.wireOp",EDGE,"E72.1");var subQ16=sQuery(id+"F12.wireOp",EDGE,"E74.1");var subQ18=sQuery(id+"F12.wireOp",EDGE,"E74.8");Q0=qUnion([makeQuery(id+"F12.imprint","IMPRINT",FACE,{"disambiguationData":[TD([[makeQuery(id+"F12.imprint","IMPRINT",EDGE,{"derivedFrom":subQ7}),1.0]])]}),makeQuery(id+"F12.imprint","IMPRINT",FACE,{"disambiguationData":[TD([[makeQuery(id+"F12.imprint","IMPRINT",EDGE,{"derivedFrom":subQ14}),1.0]])]}),makeQuery(id+"F12.imprint","IMPRINT",FACE,{"disambiguationData":[TD([[makeQuery(id+"F12.imprint","IMPRINT",EDGE,{"derivedFrom":subQ16}),1.0]])]}),makeQuery(id+"F12.imprint","IMPRINT",FACE,{"disambiguationData":[TD([[makeQuery(id+"F12.imprint","IMPRINT",EDGE,{"derivedFrom":subQ18}),-1.0]])]})]);}
            var Q1;
            Q1=makeQuery(id+"F5.boolean.opBoolean","SPLIT",FACE,{"disambiguationData":[TD([makeQuery(id+"F5.opExtrude","SWEPT_FACE",FACE,{"disambiguationData":[OSD([sQuery(id+"F4.wireOp",EDGE,"E41")])]})])],"derivedFrom":makeQuery(id+"F3.boolean.opBoolean","COPY",FACE,{"derivedFrom":makeQuery(id+"F3.opExtrude","CAP_FACE",FACE,{"disambiguationData":[OSD([sQuery(id+"F0.wireOp",EDGE,"E25.0"),sQuery(id+"F0.wireOp",EDGE,"E25.1"),sQuery(id+"F0.wireOp",EDGE,"E25.2"),sQuery(id+"F0.wireOp",EDGE,"E25.3"),sQuery(id+"F0.wireOp",EDGE,"E25.4"),sQuery(id+"F0.wireOp",EDGE,"E25.5"),sQuery(id+"F0.wireOp",EDGE,"E25.6"),sQuery(id+"F0.wireOp",EDGE,"E25.7")])],"isStart":false})})});
            extrude(context, id + "F13", {"entities" : qUnion([Q0]), "operationType" : NewBodyOperationType.REMOVE, "endBound" : BoundingType.UP_TO_SURFACE, "endBoundEntityFace" : qUnion([Q1]), "depth" : 25 * mm});
        }
        {
            var Q0;
            Q0=makeQuery(id+"F3.boolean.opBoolean","COPY",EDGE,{"derivedFrom":makeQuery(id+"F3.opExtrude","CAP_EDGE",EDGE,{"disambiguationData":[OSD([sQuery(id+"F0.wireOp",EDGE,"E25.6")])],"isStart":false})});
            var Q1;
            Q1=makeQuery(id+"F8.boolean.opBoolean","INTERSECT",EDGE,{"derivedFrom":[makeQuery(id+"F5.opExtrude","SWEPT_FACE",FACE,{"disambiguationData":[OSD([sQuery(id+"F4.wireOp",EDGE,"E30")])]}),makeQuery(id+"F8.opExtrude","CAP_FACE",FACE,{"disambiguationData":[OSD([sQuery(id+"F7.wireOp",EDGE,"E67")])],"isStart":false})]});
            var Q2;
            Q2=makeQuery(id+"F8.boolean.opBoolean","INTERSECT",EDGE,{"disambiguationData":[OD(1.0)],"derivedFrom":[makeQuery(id+"F5.opExtrude","SWEPT_FACE",FACE,{"disambiguationData":[OSD([sQuery(id+"F4.wireOp",EDGE,"E30")])]}),makeQuery(id+"F8.opExtrude","SWEPT_FACE",FACE,{"disambiguationData":[OSD([sQuery(id+"F7.wireOp",EDGE,"E67")])]})]});
            var Q3;
            {var subQ0=sQuery(id+"F4.wireOp",EDGE,"E30");Q3=makeQuery(id+"F8.boolean.opBoolean","SPLIT",EDGE,{"disambiguationData":[TD([makeQuery(id+"F5.opExtrude","SWEPT_FACE",FACE,{"disambiguationData":[OSD([sQuery(id+"F4.wireOp",EDGE,"E35.filletArc")])]})])],"derivedFrom":makeQuery(id+"F5.opExtrude","CAP_EDGE",EDGE,{"disambiguationData":[OSD([subQ0])],"isStart":false})});}
            var Q4;
            {var subQ0=sQuery(id+"F0.wireOp",EDGE,"E25.7");var subQ1=sQuery(id+"F0.wireOp",EDGE,"E25.1");var subQ2=sQuery(id+"F0.wireOp",EDGE,"E25.6");var subQ3=sQuery(id+"F0.wireOp",EDGE,"E25.5");var subQ4=sQuery(id+"F0.wireOp",EDGE,"E25.4");var subQ5=sQuery(id+"F0.wireOp",EDGE,"E25.0");var subQ6=sQuery(id+"F0.wireOp",EDGE,"E25.2");var subQ7=sQuery(id+"F0.wireOp",EDGE,"E25.3");Q4=makeQuery(id+"F8.boolean.opBoolean","INTERSECT",EDGE,{"derivedFrom":[makeQuery(id+"F5.boolean.opBoolean","SPLIT",FACE,{"disambiguationData":[TD([makeQuery(id+"F2.opExtrude","SWEPT_FACE",FACE,{"disambiguationData":[OSD([subQ5])]})])],"derivedFrom":makeQuery(id+"F3.boolean.opBoolean","COPY",FACE,{"derivedFrom":makeQuery(id+"F3.opExtrude","CAP_FACE",FACE,{"disambiguationData":[OSD([subQ5,subQ1,subQ6,subQ7,subQ4,subQ3,subQ2,subQ0])],"isStart":false})})}),makeQuery(id+"F8.opExtrude","SWEPT_FACE",FACE,{"disambiguationData":[OSD([sQuery(id+"F7.wireOp",EDGE,"E67")])]})]});}
            var Q5;
            Q5=makeQuery(id+"F8.boolean.opBoolean","INTERSECT",EDGE,{"disambiguationData":[OD(0.0)],"derivedFrom":[makeQuery(id+"F5.opExtrude","SWEPT_FACE",FACE,{"disambiguationData":[OSD([sQuery(id+"F4.wireOp",EDGE,"E30")])]}),makeQuery(id+"F8.opExtrude","SWEPT_FACE",FACE,{"disambiguationData":[OSD([sQuery(id+"F7.wireOp",EDGE,"E67")])]})]});
            fillet(context, id + "F14", {"entities" : qUnion([Q0, Q1, Q2, Q3, Q4, Q5]), "radius" : 3 * mm, "tangentPropagation" : true, "allowEdgeOverflow" : false});
        }
        {
            var Q0;
            Q0=makeQuery(id+"F1.opExtrude","CAP_EDGE",EDGE,{"disambiguationData":[OSD([sQuery(id+"F0.wireOp",EDGE,"E1.bottom")])],"isStart":false});
            fillet(context, id + "F15", {"entities" : qUnion([Q0]), "radius" : 2 * mm, "tangentPropagation" : true, "allowEdgeOverflow" : false});
        }
        {
            var Q0;
            {var subQ0=sQuery(id+"F0.wireOp",EDGE,"E21.filletArc");var subQ1=sQuery(id+"F0.wireOp",EDGE,"E7");var subQ2=sQuery(id+"F0.wireOp",EDGE,"E6");var subQ3=sQuery(id+"F0.wireOp",EDGE,"E5");var subQ4=sQuery(id+"F0.wireOp",EDGE,"E4");var subQ5=sQuery(id+"F0.wireOp",EDGE,"E22.filletArc");var subQ6=sQuery(id+"F0.wireOp",EDGE,"E1.bottom");var subQ7=sQuery(id+"F0.wireOp",EDGE,"E1.right");var subQ8=sQuery(id+"F0.wireOp",EDGE,"E1.top");var subQ9=sQuery(id+"F0.wireOp",EDGE,"E1.left");var subQ10=sQuery(id+"F0.wireOp",EDGE,"E23.filletArc");var subQ11=sQuery(id+"F0.wireOp",EDGE,"E24.filletArc");Q0=makeQuery(id+"F2.boolean.opBoolean","SPLIT",FACE,{"disambiguationData":[TD([makeQuery(id+"F1.opExtrude","SWEPT_FACE",FACE,{"disambiguationData":[OSD([subQ6])]})])],"derivedFrom":makeQuery(id+"F1.opExtrude","CAP_FACE",FACE,{"disambiguationData":[OSD([subQ6,subQ8,subQ9,subQ7,subQ4,subQ3,subQ2,subQ1,subQ0,subQ5,subQ10,subQ11])],"isStart":true})});}
            var sketch = newSketch(context, id + "F16", { "sketchPlane" : qUnion([Q0])});
            skLineSegment(sketch, "E79", {"start": v(0, 74.25) * mm, "end": v(0, 120) * mm, "construction": true});
            skCircle(sketch, "E80", {"center": v(0, 120) * mm, "radius": 6 * mm});
            skLineSegment(sketch, "E81", {"start": v(-74.25, 0) * mm, "end": v(74.25, 0) * mm});
            skArc(sketch, "E82", {"start": v(15, 120) * mm, "mid": v(0, 135) * mm, "end": v(-15, 120) * mm});
            skLineSegment(sketch, "E83", {"start": v(-15, 108) * mm, "end": v(-33, 90) * mm});
            skLineSegment(sketch, "E84", {"start": v(-15, 120) * mm, "end": v(-15, 108) * mm});
            skLineSegment(sketch, "E85", {"start": v(15, 120) * mm, "end": v(15, 108) * mm});
            skLineSegment(sketch, "E86", {"start": v(15, 108) * mm, "end": v(33, 90) * mm});
            skLineSegment(sketch, "E87.MirrorCS", {"start": v(-15, -120) * mm, "end": v(-15, -108) * mm});
            skLineSegment(sketch, "E88.MirrorCS", {"start": v(15, -120) * mm, "end": v(15, -108) * mm});
            skArc(sketch, "E89.MirrorCS", {"start": v(15, -120) * mm, "mid": v(0, -135) * mm, "end": v(-15, -120) * mm});
            skLineSegment(sketch, "E90.MirrorCS", {"start": v(15, -108) * mm, "end": v(33, -90) * mm});
            skLineSegment(sketch, "E91.MirrorCS", {"start": v(-15, -108) * mm, "end": v(-33, -90) * mm});
            skCircle(sketch, "E92.MirrorC", {"center": v(0, -120) * mm, "radius": 6 * mm});
            skLineSegment(sketch, "E93.MirrorCS", {"start": v(0, -74.25) * mm, "end": v(0, -120) * mm, "construction": true});
            skSolve(sketch);
        }
        {
            var Q0;
            Q0=makeQuery(id+"F16.imprint","IMPRINT",FACE,{"disambiguationData":[TD([[makeQuery(id+"F16.imprint","IMPRINT",EDGE,{"derivedFrom":sQuery(id+"F16.wireOp",EDGE,"E87.MirrorCS")}),-1.0]])]});
            var Q1;
            Q1=makeQuery(id+"F16.imprint","IMPRINT",FACE,{"disambiguationData":[TD([[makeQuery(id+"F16.imprint","IMPRINT",EDGE,{"derivedFrom":makeQuery(id+"F1.opExtrude","CAP_EDGE",EDGE,{"disambiguationData":[OSD([sQuery(id+"F0.wireOp",EDGE,"E6")])],"isStart":true})}),-1.0]])]});
            var Q2;
            Q2=makeQuery(id+"F16.imprint","IMPRINT",FACE,{"disambiguationData":[TD([[makeQuery(id+"F16.imprint","IMPRINT",EDGE,{"derivedFrom":makeQuery(id+"F1.opExtrude","CAP_EDGE",EDGE,{"disambiguationData":[OSD([sQuery(id+"F0.wireOp",EDGE,"E4")])],"isStart":true})}),-1.0]])]});
            var Q3;
            Q3=makeQuery(id+"F16.imprint","IMPRINT",FACE,{"disambiguationData":[TD([[makeQuery(id+"F16.imprint","IMPRINT",EDGE,{"derivedFrom":sQuery(id+"F16.wireOp",EDGE,"E80")}),-1.0]])]});
            extrude(context, id + "F17", {"entities" : qUnion([Q0, Q1, Q2, Q3]), "depth" : 3 * mm, "offsetDistance" : 25 * mm});
        }
    });
